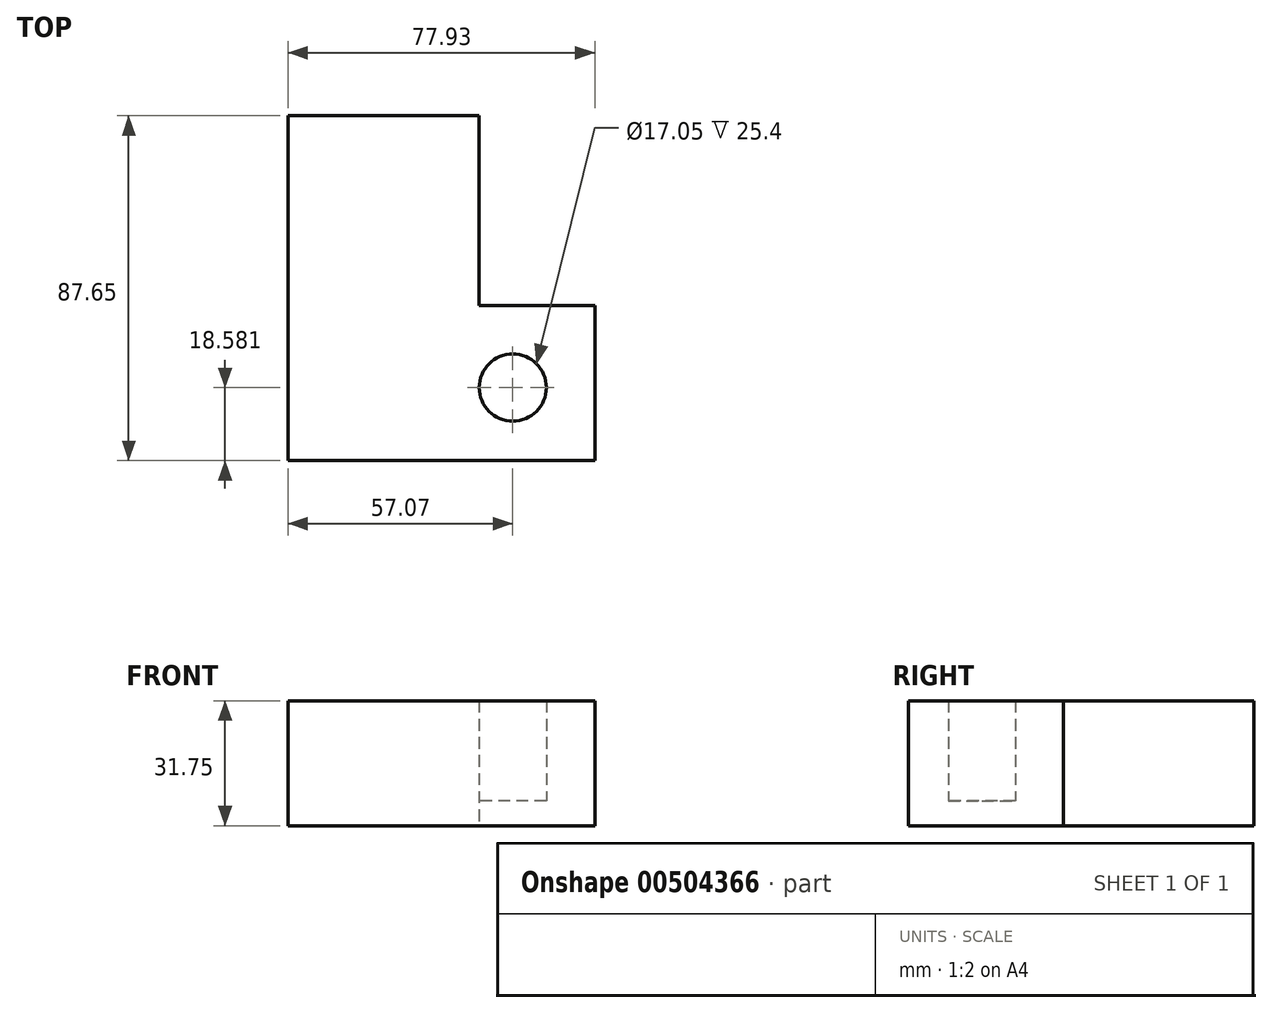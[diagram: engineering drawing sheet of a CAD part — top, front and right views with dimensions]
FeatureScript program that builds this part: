
annotation { "Feature Type Name" : "Feature", "Feature Type Description" : "" }
export const myFeature = defineFeature(function(context is Context, id is Id, definition is map)
    precondition{}
    {
        {
            var Q0;
            Q0=qCreatedBy(makeId("Top.planeOp"),FACE);
            var sketch = newSketch(context, id + "F0", { "sketchPlane" : qUnion([Q0])});
            skLineSegment(sketch, "E0", {"start": v(0, 0) * mm, "end": v(77.93, 0) * mm});
            skLineSegment(sketch, "E1", {"start": v(77.93, 0) * mm, "end": v(77.93, 39.37) * mm});
            skLineSegment(sketch, "E2", {"start": v(77.93, 39.37) * mm, "end": v(48.54, 39.37) * mm});
            skLineSegment(sketch, "E3", {"start": v(48.54, 39.37) * mm, "end": v(48.54, 87.65) * mm});
            skLineSegment(sketch, "E4", {"start": v(48.54, 87.65) * mm, "end": v(0, 87.65) * mm});
            skLineSegment(sketch, "E5", {"start": v(0, 87.65) * mm, "end": v(0, 0) * mm});
            skSolve(sketch);
        }
        {
            var Q0;
            Q0=makeQuery(id+"F0.imprint","IMPRINT",FACE,{"disambiguationData":[TD([[makeQuery(id+"F0.imprint","IMPRINT",EDGE,{"derivedFrom":sQuery(id+"F0.wireOp",EDGE,"E0")}),1.0]])]});
            extrude(context, id + "F1", {"entities" : qUnion([Q0]), "depth" : 6.35 * mm});
        }
        {
            var Q0;
            Q0=makeQuery(id+"F1.opExtrude","CAP_FACE",FACE,{"disambiguationData":[OSD([sQuery(id+"F0.wireOp",EDGE,"E0"),sQuery(id+"F0.wireOp",EDGE,"E1"),sQuery(id+"F0.wireOp",EDGE,"E2"),sQuery(id+"F0.wireOp",EDGE,"E3"),sQuery(id+"F0.wireOp",EDGE,"E4"),sQuery(id+"F0.wireOp",EDGE,"E5")])],"isStart":false});
            var sketch = newSketch(context, id + "F2", { "sketchPlane" : qUnion([Q0])});
            skCircle(sketch, "E6", {"center": v(57.07, 18.58) * mm, "radius": 8.53 * mm});
            skSolve(sketch);
        }
        {
            var Q0;
            Q0=makeQuery(id+"F2.imprint","IMPRINT",FACE,{"disambiguationData":[TD([[makeQuery(id+"F2.imprint","IMPRINT",EDGE,{"derivedFrom":sQuery(id+"F2.wireOp",EDGE,"E6")}),-1.0]])]});
            extrude(context, id + "F3", {"entities" : qUnion([Q0]), "operationType" : NewBodyOperationType.ADD, "depth" : 25.4 * mm});
        }
    });
